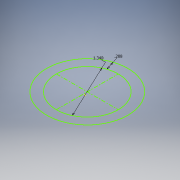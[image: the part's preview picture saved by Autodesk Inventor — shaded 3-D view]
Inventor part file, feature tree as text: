
AUTODESK INVENTOR PART (.ipt)
format: ipt  version: 2016 (Build 200138000, 138)  size: 83,456 bytes
history: native  units: in
note: dims shown in document units (in); Inventor stores cm internally (conversion verified against a paired STEP export)
features: sketch x1
ambient origin geometry x8: Origin, YZ Plane, XZ Plane, XY Plane, X Axis, Y Axis, Z Axis, Center Point
feature tree (1):
  sketch  "Sketch1"  dims[d2=1.34in d4=0.2075in]
